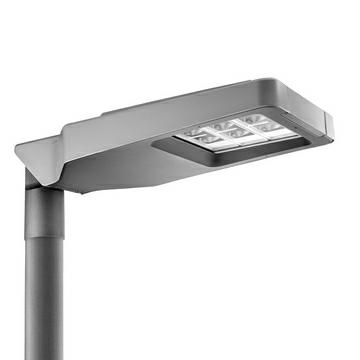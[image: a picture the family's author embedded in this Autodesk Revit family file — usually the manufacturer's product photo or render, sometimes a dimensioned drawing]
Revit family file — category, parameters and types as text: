
# Revit family: Lighting-StreetLighting-GEWISS-ROAD[5]MINI-LED_OPTIC_HUGE_CLII
name_source: partatom
category: Apparecchi per illuminazione
units: mm (PartAtom-declared; Revit-internal decimal feet)

## family parameters
Basato su piano di lavoro = No
Condiviso = No
Punto di calcolo locali = No
Quota connettore circolare = Usa diametro
Sempre verticale = Sì
Sorgente d'illuminazione = No
Taglio con vuoti quando caricato = No
Tipo di parte = Normale

## types (35) — shared parameters
Applicazione = External
Carico apparente = 53 VA
Catalogue = LIGHTING
Catalogue Range = ROAD [5]
Commenti sul wattaggio = 53W
Electrocod = 244C
IDF = 99241b9b-65a6-420a-b558-f156d6702ffc
IDT = 71f3a6385bd246d58e1a34223c0a3191
IP degree = IP66
Immagine tipo = GWR5276M.jpg
Insulation class = II
Lamp- = LED
Lampada = LED
Minimum distance from the illuminated object = 1M
Produttore = GEWISS S.p.A.
SEO = Street lighting
Shock resistance = IK08
Technical sheet = https://www.gewiss.com
Tilt adjustable = -20° ÷ +10° side bracket - -10° ÷ +20° pole head
URL = https://www.gewiss.com
Version file RFA = 20.11
Warranty = 5 years

## per-type parameters (varying)
- GWR5172M30K - ROAD5 MINI HUGE 2M 3000K 0,7A CL2 1-10V: Body=Die-cast aluminium -; Classification:=-; Color Rendering Index=CRI-70; Colore=Graphite grey; Colour :=Powder coating; Colour temperature=3000K; Colour temperature:=3000 K (CRI>80); Context=Street and parking lighting; Control System=Dimmable 1-10 V; DIN 18032-3 certification=-; Descrizione=GWR5172M30K - ROAD5 MINI HUGE 2M 3000K 0,7A CL2 1-10V; Device with reduced surface temperature=-; Driver=Included; Driver Box=Built-in; Efficiency (lm/W)=96; Eletrical and lighting features=-; External screw=Stainless steel; Fixing=Pole Head - Outreach; Gasket=Anti-aging silicone; General information=-; Glow Wire Test :=-; IPEA=ROAD = A ++ // LARGE AREAS = A ++ // CYCLOPEDONALS = A + // GREEN AREAS = A + // HISTORICAL CENTER = A5 +; Installationa and maintenance=-; LED Life Time (L80B05)=77000H; LED Maintenance=Not available; LED current.=0,7A; Lifetime=L90B10 (Tq+25°C) = 100.000 h - L90B10 (Tq+50°C) = 75.000 h; Locking Hook=Integrated front handle; Lumen output (lm)=5200; Luminaire=LED Road Equipment; Materials=-; Maximum surface exposed to the wind=0,149999999999999M2; Maximum surface exposed to the wind :=0.15 m²; Modello=GWR5172M30K; Mouting and installation=Pole Head - Outreach; Nominal flux (lm)=5400; Number of modules=2 (2x3 LED); Operating temperature :=-25 +50 °C; Operating temperature:=-25 +50 °C; Optic=HUGE; Optic :=Metallized polycarbonate reflector; Optic Maintenance=Not available; Optic and illuminating features=-; Overvoltage protection=DM 10KV / CM 10KV; Overvoltage resistance :=Common and dfferential mode: 10KV; Photobiological Risk Class=RG0; Power supply operation=Dimmable; Rated frequency (Hz)=50 / 60; Shield type=4mm thick flat tempered glass; Standard Deviation Colour Matching=SDCM = 5; Standard-=EN 60598-2-3, EN 60598-1 IEC/TR 62778; Standards and approvals=-; Stocking temperature=-; Supply voltage=220 - 240 V; System power=53W; System power :=54 W @ 0.7A; Tilt-=-20° ÷ +10° side bracket - -10° ÷ +20° pole head; Tipo alimentatore=Constant Current Driver Led; Tipologia=Dimmable; Type of light source=LED - Not replaceable; Unified Glare Rating=G*3 - ULOR = 0; Unique digital code (Datamatrix)=Currently not present; Voltage-=220/240 V - 50/60 Hz - Dimmable 1-10 V; Weight (kg):=6,6; Wiring=Isolating switch
- GWR5112 - ROAD 5 2M 4000K 1A OPT.ST1: Colour temperature=4000 K (CRI 70); Colour temperature:=4000 K (CRI 70); Descrizione=ROAD 5 2M 4000K 1A OPT.ST1; EAN code=8011564857711; LED LifeTime (L80B05)=120000H; LED current.=1A; Lumen output (lm)=6730; Maximum surface exposed to the wind=0,15M2; Modello=GWR5112; No. Chorus modules=2 (2x3 LED); Nominal flux (lm)=9540; Number of modules=2 (2x3 LED); Operating temperature:=-25 +40 °C; Optic=H - ULOR: 0%; Overvoltage resistance=12 KV (Common and dfferential mode); Pilot current=1A; System power=76W; Tipo alimentatore=Constant Current Driver Led; Tipologia=Stand alone; Voltage-=220/240 V - 50/60 Hz - Stand alone; Weight (kg)=6,6; Weight (kg):=6,6; Working temperature=-25 +40 °C
- GWR5111B - ROAD 5 BI-POW.1M 4000K 1A OPT.ST1: Colour temperature=4000 K (CRI 70); Colour temperature:=4000 K (CRI 70); Descrizione=ROAD 5 BI-POW.1M 4000K 1A OPT.ST1; EAN code=8011564857735; LED LifeTime (L80B05)=120000H; LED current.=1A; Lumen output (lm)=3370; Maximum surface exposed to the wind=0,15M2; Modello=GWR5111B; No. Chorus modules=1 (1x3 LED); Nominal flux (lm)=4770; Number of modules=1 (1x3 LED); Operating temperature:=-25 +40 °C; Optic=H - ULOR: 0%; Overvoltage resistance=12 KV (Common and dfferential mode); Pilot current=1A; Power supply operation=Bi power; System power=39W; Tipo alimentatore=Constant Current Driver Led; Tipologia=Bi power; Voltage-=220/240 V - 50/60 Hz - Bi-power with self-learning; Weight (kg)=6,4; Weight (kg):=6,4; Working temperature=-25 +40 °C
- GWR5112M30K - ROAD5 MINI HUGE 2M 3000K 1,0A CL2 1-10V: Body=Die-cast aluminium -; Classification:=-; Color Rendering Index=CRI-70; Colore=Graphite grey; Colour :=Powder coating; Colour temperature=3000K; Colour temperature:=3000 K (CRI>80); Context=Street and parking lighting; Control System=Dimmable 1-10 V; DIN 18032-3 certification=-; Descrizione=GWR5112M30K - ROAD5 MINI HUGE 2M 3000K 1,0A CL2 1-10V; Device with reduced surface temperature=-; Driver=Included; Driver Box=Built-in; Efficiency (lm/W)=91; Eletrical and lighting features=-; External screw=Stainless steel; Fixing=Pole Head - Outreach; Gasket=Anti-aging silicone; General information=-; Glow Wire Test :=-; IPEA=ROAD = A + // LARGE AREAS = A + // CYCLOPEDONALS = A // GREEN AREAS = A // HISTORICAL CENTER = A4 +; Installationa and maintenance=-; LED Life Time (L80B05)=120000H; LED Maintenance=Not available; LED current.=1A; Lifetime=L90B10 (Tq+25°C) = 100.000 h - L90B10 (Tq+40°C) = 75.000 h; Locking Hook=Integrated front handle; Lumen output (lm)=7000; Luminaire=LED Road Equipment; Materials=-; Maximum surface exposed to the wind=0,149999999999999M2; Maximum surface exposed to the wind :=0.15 m²; Modello=GWR5112M30K; Mouting and installation=Pole Head - Outreach; Nominal flux (lm)=8280; Number of modules=2 (2x3 LED); Operating temperature :=-25 +40 °C; Operating temperature:=-25 +40 °C; Optic=HUGE; Optic :=Metallized polycarbonate reflector; Optic Maintenance=Not available; Optic and illuminating features=-; Overvoltage protection=DM 10KV / CM 10KV; Overvoltage resistance :=Common and dfferential mode: 10KV; Photobiological Risk Class=RG0; Power supply operation=Dimmable; Rated frequency (Hz)=50 / 60; Shield type=4mm thick flat tempered glass; Standard Deviation Colour Matching=SDCM = 5; Standard-=EN 60598-2-3, EN 60598-1 IEC/TR 62778; Standards and approvals=-; Stocking temperature=-; Supply voltage=220 - 240 V; System power=76W; System power :=77 W @ 1A; Tilt-=-20° ÷ +10° side bracket - -10° ÷ +20° pole head; Tipo alimentatore=Constant Current Driver Led; Tipologia=Dimmable; Type of light source=LED - Not replaceable; Unified Glare Rating=G*3 - ULOR = 0; Unique digital code (Datamatrix)=Currently not present; Voltage-=220/240 V - 50/60 Hz - Dimmable 1-10 V; Weight (kg):=6,6; Wiring=Isolating switch
- GWR5171V - ROAD5 MINI HUGE V 1M 4000K 0,7A CL2: Body=Die-cast aluminium -; Classification:=-; Color Rendering Index=CRI-70; Colore=Graphite grey; Colour :=Powder coating; Colour temperature=4000K; Colour temperature:=4000 K (CRI>70); Context=Street and parking lighting; Control System=DALI - 5 Step; DIN 18032-3 certification=-; Descrizione=GWR5171V - ROAD5 MINI HUGE V 1M 4000K 0,7A CL2; Device with reduced surface temperature=-; Driver=Included; Driver Box=Built-in; Efficiency (lm/W)=107; Eletrical and lighting features=-; External screw=Stainless steel; Fixing=Pole Head - Outreach; Gasket=Anti-aging silicone; General information=-; Glow Wire Test :=-; IPEA=ROAD = A3 + // LARGE AREAS = A4 + // CYCLOPEDONALS = A3 + // GREEN AREAS = A3 + // HISTORICAL CENTER = A6 +; Installationa and maintenance=-; LED Life Time (L80B05)=120000H; LED Maintenance=Not available; LED current.=0,7A; Lifetime=L90B10 (Tq+25°C) = 100.000 h - L90B10 (Tq+50°C) = 75.000 h; Locking Hook=Integrated front handle; Lumen output (lm)=3000; Luminaire=LED Road Equipment; Materials=-; Maximum surface exposed to the wind=0,149999999999999M2; Maximum surface exposed to the wind :=0.15 m²; Modello=GWR5171V; Mouting and installation=Pole Head - Outreach; Nominal flux (lm)=3120; Number of modules=1 (1x3 LED); Operating temperature :=-25 +50 °C; Operating temperature:=-25 +40 °C; Optic=HUGE; Optic :=Metallized polycarbonate reflector; Optic Maintenance=Not available; Optic and illuminating features=-; Overvoltage protection=DM 10KV / CM 10KV; Photobiological Risk Class=RG0; Rated frequency (Hz)=50 / 60; Shield type=4mm thick flat tempered glass; Standard Deviation Colour Matching=SDCM = 5; Standard-=EN 60598-2-3, EN 60598-1 IEC/TR 62778; Standards and approvals=-; Stocking temperature=-; Supply voltage=220 - 240 V; System power=27W; System power :=28 W @ 0.7A; Tilt-=-20° ÷ +10° side bracket - -10° ÷ +20° pole head; Tipologia=Programmable (5 step); Type of light source=LED - Not replaceable; Unified Glare Rating=G*3 - ULOR = 0; Unique digital code (Datamatrix)=Currently not present; Voltage-=220/240 V - 50/60 Hz - Stand alone and/or programmable; Weight (kg):=6,4; Wiring=Isolating switch
- GWR5172B - ROAD5 MINI HUGE 2M 4000K 0,7A CL2 BIREG: Colour temperature=4000 K (CRI 70); Colour temperature:=4000 K (CRI 70); Descrizione=ROAD 5 BI-POW.2M 4000K 700mA OPT.ST1; EAN code=8011564857742; LED LifeTime (L80B05)=77000H; LED current.=0,7A; Lumen output (lm)=4590; Maximum surface exposed to the wind=0,15M2; Modello=GWR5172B; No. Chorus modules=2 (2x3 LED); Nominal flux (lm)=6240; Number of modules=2 (2x3 LED); Operating temperature:=-25 +50 °C; Optic=H - ULOR: 0%; Overvoltage resistance=12 KV (Common and dfferential mode); Pilot current=0,7A; Power supply operation=Bi power; System power=54W; Tipo alimentatore=Constant Current Driver Led; Tipologia=Bi power; Voltage-=220/240 V - 50/60 Hz - Bi-power with self-learning; Weight (kg)=6,6; Weight (kg):=6,6; Working temperature=-25 +50 °C
- GWR511230K - ROAD 5 2M 3000K 1A OTT.ST1: Body=Die-cast aluminium -; Classification:=-; Color Rendering Index=CRI-70; Colore=Graphite grey; Colour :=Powder coating; Colour temperature=3000K; Colour temperature:=3000 K (CRI>80); Context=Street and parking lighting; Control System=Stand alone; DIN 18032-3 certification=-; Descrizione=GWR511230K - ROAD 5 2M 3000K 1A OTT.ST1; Device with reduced surface temperature=-; Driver=Included; Driver Box=Built-in; Efficiency (lm/W)=97; Eletrical and lighting features=-; External screw=Stainless steel; Fixing=Pole Head - Outreach; Gasket=Anti-aging silicone; General information=-; Glow Wire Test :=-; IPEA=ROAD = A + // LARGE AREAS = A ++ // CYCLOPEDONALS = A + // GREEN AREAS = A + // HISTORICAL CENTER = A5 +; Installationa and maintenance=-; LED Life Time (L80B05)=120000H; LED Maintenance=Not available; LED current.=0,9A; Lifetime=L90B10 (Tq+25°C) = 100.000 h - L90B10 (Tq+40°C) = 75.000 h; Locking Hook=Integrated front handle; Lumen output (lm)=6500; Luminaire=LED Road Equipment; Materials=-; Maximum surface exposed to the wind=0,149999999999999M2; Maximum surface exposed to the wind :=0.15 m²; Modello=GWR511230K; Mouting and installation=Pole Head - Outreach; Nominal flux (lm)=8280; Number of modules=2 (2x3 LED); Operating temperature :=-25 +40 °C; Operating temperature:=-25 +40 °C; Optic=HUGE; Optic :=Metallized polycarbonate reflector; Optic Maintenance=Not available; Optic and illuminating features=-; Overvoltage protection=DM 10KV / CM 10KV; Overvoltage resistance :=Common and dfferential mode: 10KV; Photobiological Risk Class=RG0; Rated frequency (Hz)=50 / 60; Shield type=4mm thick flat tempered glass; Standard Deviation Colour Matching=SDCM = 5; Standard-=EN 60598-2-3, EN 60598-1 IEC/TR 62778; Standards and approvals=-; Stocking temperature=-; Supply voltage=220 - 240 V; System power=76W; System power :=67 W @ 0.9A; Tilt-=-20° ÷ +10° side bracket - -10° ÷ +20° pole head; Tipo alimentatore=Constant Current Driver Led; Tipologia=Stand alone; Type of light source=LED - Not replaceable; Unified Glare Rating=G*3 - ULOR = 0; Unique digital code (Datamatrix)=Currently not present; Voltage-=220/240 V - 50/60 Hz - Stand alone; Weight (kg):=6,6; Wiring=Isolating switch
- GWR5131 - ROAD5 MINI HUGE 1M 4000K 0,35A CL2: Colour temperature=4000 K (CRI 70); Colour temperature:=4000 K (CRI 70); Descrizione=ROAD5 MINI HUGE 1M 4000K 0,35A CL2; EAN code=8011564874022; LED LifeTime (L80B05)=77000H; LED current.=0,35A; Lumen output (lm)=1150; Maximum surface exposed to the wind=0,15M2; Modello=GWR5131; No. Chorus modules=1 (1x3 LED); Nominal flux (lm)=1560; Number of modules=1 (1x3 LED); Operating temperature:=-25 +50 °C; Optic=H - ULOR: 0%; Overvoltage resistance=12 KV (Common and dfferential mode); Pilot current=0,35A; System power=14W; Tipo alimentatore=Constant Current Driver Led; Tipologia=Stand alone; Voltage-=220/240 V - 50/60 Hz - Stand alone; Weight (kg)=6,4; Weight (kg):=6,4; Working temperature=-25 +50 °C
- GWR5112B - ROAD 5 BI-POW.2M 4000K 1A OPT.ST1: Colour temperature=4000 K (CRI 70); Colour temperature:=4000 K (CRI 70); Descrizione=ROAD 5 BI-POW.2M 4000K 1A OPT.ST1; EAN code=8011564857759; LED LifeTime (L80B05)=120000H; LED current.=1A; Lumen output (lm)=6730; Maximum surface exposed to the wind=0,15M2; Modello=GWR5112B; No. Chorus modules=2 (2x3 LED); Nominal flux (lm)=9540; Number of modules=2 (2x3 LED); Operating temperature:=-25 +40 °C; Optic=H - ULOR: 0%; Overvoltage resistance=12 KV (Common and dfferential mode); Pilot current=1A; Power supply operation=Bi power; System power=77W; Tipo alimentatore=Constant Current Driver Led; Tipologia=Bi power; Voltage-=220/240 V - 50/60 Hz - Bi-power with self-learning; Weight (kg)=6,6; Weight (kg):=6,6; Working temperature=-25 +40 °C
- GWR5172B30K - ROAD5 MINI HUGE 2M 3000K 0,7A CL2 BIREG: Body=Die-cast aluminium -; Classification:=-; Color Rendering Index=CRI-70; Colore=Graphite grey; Colour :=Powder coating; Colour temperature=3000K; Colour temperature:=3000 K (CRI>80); Context=Street and parking lighting; Control System=Bi-power with self-learning; DIN 18032-3 certification=-; Descrizione=GWR5172B30K - ROAD5 MINI HUGE 2M 3000K 0,7A CL2 BIREG; Device with reduced surface temperature=-; Driver=Included; Driver Box=Built-in; Efficiency (lm/W)=96; Eletrical and lighting features=-; External screw=Stainless steel; Fixing=Pole Head - Outreach; Gasket=Anti-aging silicone; General information=-; Glow Wire Test :=-; IPEA=ROAD = A ++ // LARGE AREAS = A ++ // CYCLOPEDONALS = A + // GREEN AREAS = A + // HISTORICAL CENTER = A5 +; Installationa and maintenance=-; LED Life Time (L80B05)=77000H; LED Maintenance=Not available; LED current.=0,7A; Lifetime=L90B10 (Tq+25°C) = 100.000 h - L90B10 (Tq+50°C) = 75.000 h; Locking Hook=Integrated front handle; Lumen output (lm)=5200; Luminaire=LED Road Equipment; Materials=-; Maximum surface exposed to the wind=0,149999999999999M2; Maximum surface exposed to the wind :=0.15 m²; Modello=GWR5172B30K; Mouting and installation=Pole Head - Outreach; Nominal flux (lm)=5400; Number of modules=2 (2x3 LED); Operating temperature :=-25 +50 °C; Operating temperature:=-25 +50 °C; Optic=HUGE; Optic :=Metallized polycarbonate reflector; Optic Maintenance=Not available; Optic and illuminating features=-; Overvoltage protection=DM 10KV / CM 10KV; Overvoltage resistance :=Common and dfferential mode: 10KV; Photobiological Risk Class=RG0; Power supply operation=Bi power; Rated frequency (Hz)=50 / 60; Shield type=4mm thick flat tempered glass; Standard Deviation Colour Matching=SDCM = 5; Standard-=EN 60598-2-3, EN 60598-1 IEC/TR 62778; Standards and approvals=-; Stocking temperature=-; Supply voltage=220 - 240 V; System power=54W; System power :=54 W @ 0.7A; Tilt-=-20° ÷ +10° side bracket - -10° ÷ +20° pole head; Tipo alimentatore=Constant Current Driver Led; Tipologia=Bi power; Type of light source=LED - Not replaceable; Unified Glare Rating=G*3 - ULOR = 0; Unique digital code (Datamatrix)=Currently not present; Voltage-=220/240 V - 50/60 Hz - Bi-power with self-learning; Weight (kg):=6,6; Wiring=Isolating switch
- GWR517230K - ROAD5 MINI HUGE 2M 3000K 0,7A CL2: Body=Die-cast aluminium -; Classification:=-; Color Rendering Index=CRI-70; Colore=Graphite grey; Colour :=Powder coating; Colour temperature=3000K; Colour temperature:=3000 K (CRI>80); Context=Street and parking lighting; Control System=Stand alone; DIN 18032-3 certification=-; Descrizione=GWR517230K - ROAD5 MINI HUGE 2M 3000K 0,7A CL2; Device with reduced surface temperature=-; Driver=Included; Driver Box=Built-in; Efficiency (lm/W)=98; Eletrical and lighting features=-; External screw=Stainless steel; Fixing=Pole Head - Outreach; Gasket=Anti-aging silicone; General information=-; Glow Wire Test :=-; IPEA=ROAD = A ++ // LARGE AREAS = A3 + // CYCLOPEDONALS = A ++ // GREEN AREAS = A ++ // HISTORICAL CENTER = A5 +; Installationa and maintenance=-; LED Life Time (L80B05)=77000H; LED Maintenance=Not available; LED current.=0,7A; Lifetime=L90B10 (Tq+25°C) = 100.000 h - L90B10 (Tq+50°C) = 75.000 h; Locking Hook=Integrated front handle; Lumen output (lm)=5200; Luminaire=LED Road Equipment; Materials=-; Maximum surface exposed to the wind=0,149999999999999M2; Maximum surface exposed to the wind :=0.15 m²; Modello=GWR517230K; Mouting and installation=Pole Head - Outreach; Nominal flux (lm)=5400; Number of modules=2 (2x3 LED); Operating temperature :=-25 +50 °C; Operating temperature:=-25 +50 °C; Optic=HUGE; Optic :=Metallized polycarbonate reflector; Optic Maintenance=Not available; Optic and illuminating features=-; Overvoltage protection=DM 10KV / CM 10KV; Overvoltage resistance :=Common and dfferential mode: 10KV; Photobiological Risk Class=RG0; Rated frequency (Hz)=50 / 60; Shield type=4mm thick flat tempered glass; Standard Deviation Colour Matching=SDCM = 5; Standard-=EN 60598-2-3, EN 60598-1 IEC/TR 62778; Standards and approvals=-; Stocking temperature=-; Supply voltage=220 - 240 V; System power=53W; System power :=53 W @ 0.7A; Tilt-=-20° ÷ +10° side bracket - -10° ÷ +20° pole head; Tipo alimentatore=Constant Current Driver Led; Tipologia=Stand alone; Type of light source=LED - Not replaceable; Unified Glare Rating=G*3 - ULOR = 0; Unique digital code (Datamatrix)=Currently not present; Voltage-=220/240 V - 50/60 Hz - Stand alone; Weight (kg):=6,6; Wiring=Isolating switch
- GWR5171B - ROAD5 MINI HUGE 1M 4000K 0,7A CL2 BIREG: Colour temperature=4000 K (CRI 70); Colour temperature:=4000 K (CRI 70); Descrizione=ROAD 5 BI-POW.1M 4000K 700mA OPT.ST1; EAN code=8011564857728; LED LifeTime (L80B05)=77000H; LED current.=0,7A; Lumen output (lm)=2300; Maximum surface exposed to the wind=0,15M2; Modello=GWR5171B; No. Chorus modules=1 (1x3 LED); Nominal flux (lm)=3120; Number of modules=1 (1x3 LED); Operating temperature:=-25 +50 °C; Optic=H - ULOR: 0%; Overvoltage resistance=12 KV (Common and dfferential mode); Pilot current=0,7A; Power supply operation=Bi power; System power=28W; Tipo alimentatore=Constant Current Driver Led; Tipologia=Bi power; Voltage-=220/240 V - 50/60 Hz - Bi-power with self-learning; Weight (kg)=6,4; Weight (kg):=6,4; Working temperature=-25 +50 °C
- GWR5111M - ROAD5 MINI HUGE 1M 4000K 1,0A CL2 1-10V: Colour temperature=4000 K (CRI 70); Colour temperature:=4000 K (CRI 70); Descrizione=ROAD 5 DIMM.1M 4000K 1A OPT.ST1; EAN code=8011564857773; LED LifeTime (L80B05)=120000H; LED current.=1A; Lumen output (lm)=3370; Maximum surface exposed to the wind=0,15M2; Modello=GWR5111M; No. Chorus modules=1 (1x3 LED); Nominal flux (lm)=4770; Number of modules=1 (1x3 LED); Operating temperature:=-25 +40 °C; Optic=H - ULOR: 0%; Overvoltage resistance=12 KV (Common and dfferential mode); Pilot current=1A; Power supply operation=Dimmable; System power=38W; Tipo alimentatore=Constant Current Driver Led; Tipologia=Dimmable; Voltage-=220/240 V - 50/60 Hz - Dimmable 1-10 V; Weight (kg)=6,4; Weight (kg):=6,4; Working temperature=-25 +40 °C
- GWR511130K - ROAD 5 1M 3000K 1A OTT.ST1: Body=Die-cast aluminium -; Classification:=-; Color Rendering Index=CRI-70; Colore=Graphite grey; Colour :=Powder coating; Colour temperature=3000K; Colour temperature:=3000 K (CRI>80); Context=Street and parking lighting; Control System=Stand alone; DIN 18032-3 certification=-; Descrizione=GWR511130K - ROAD 5 1M 3000K 1A OTT.ST1; Device with reduced surface temperature=-; Driver=Included; Driver Box=Built-in; Efficiency (lm/W)=92; Eletrical and lighting features=-; External screw=Stainless steel; Fixing=Pole Head - Outreach; Gasket=Anti-aging silicone; General information=-; Glow Wire Test :=-; IPEA=ROAD = A + // LARGE AREAS = A ++ // CYCLOPEDONALS = A + // GREEN AREAS = A + // HISTORICAL CENTER = A4 +; Installationa and maintenance=-; LED Life Time (L80B05)=120000H; LED Maintenance=Not available; LED current.=1A; Lifetime=L90B10 (Tq+25°C) = 100.000 h - L90B10 (Tq+40°C) = 75.000 h; Locking Hook=Integrated front handle; Lumen output (lm)=3500; Luminaire=LED Road Equipment; Materials=-; Maximum surface exposed to the wind=0,149999999999999M2; Maximum surface exposed to the wind :=0.15 m²; Modello=GWR511130K; Mouting and installation=Pole Head - Outreach; Nominal flux (lm)=4140; Number of modules=1 (1x3 LED); Operating temperature :=-25 +40 °C; Operating temperature:=-25 +40 °C; Optic=HUGE; Optic :=Metallized polycarbonate reflector; Optic Maintenance=Not available; Optic and illuminating features=-; Overvoltage protection=DM 10KV / CM 10KV; Overvoltage resistance :=Common and dfferential mode: 10KV; Photobiological Risk Class=RG0; Rated frequency (Hz)=50 / 60; Shield type=4mm thick flat tempered glass; Standard Deviation Colour Matching=SDCM = 5; Standard-=EN 60598-2-3, EN 60598-1 IEC/TR 62778; Standards and approvals=-; Stocking temperature=-; Supply voltage=220 - 240 V; System power=38W; System power :=38 W @ 1A; Tilt-=-20° ÷ +10° side bracket - -10° ÷ +20° pole head; Tipo alimentatore=Constant Current Driver Led; Tipologia=Stand alone; Type of light source=LED - Not replaceable; Unified Glare Rating=G*3 - ULOR = 0; Unique digital code (Datamatrix)=Currently not present; Voltage-=220/240 V - 50/60 Hz - Stand alone; Weight (kg):=6,4; Wiring=Isolating switch
- GWR5171 - ROAD 5 1M 4000K 700mA OPT.ST1: Colour temperature=4000 K (CRI 70); Colour temperature:=4000 K (CRI 70); Descrizione=ROAD 5 1M 4000K 700mA OPT.ST1; EAN code=8011564857377; LED LifeTime (L80B05)=77000H; LED current.=0,7A; Lumen output (lm)=2300; Maximum surface exposed to the wind=0,15M2; Modello=GWR5171; No. Chorus modules=1 (1x3 LED); Nominal flux (lm)=3120; Number of modules=1 (1x3 LED); Operating temperature:=-25 +50 °C; Optic=H - ULOR: 0%; Overvoltage resistance=12 KV (Common and dfferential mode); Pilot current=0,7A; System power=27W; Tipo alimentatore=Constant Current Driver Led; Tipologia=Stand alone; Voltage-=220/240 V - 50/60 Hz - Stand alone; Weight (kg)=6,4; Weight (kg):=6,4; Working temperature=-25 +50 °C
- GWR5171M - ROAD5 MINI HUGE 1M 4000K 0,7A CL2 1-10V: Colour temperature=4000 K (CRI 70); Colour temperature:=4000 K (CRI 70); Descrizione=ROAD 5 DIMM.1M 4000K 700mA OPT.ST1; EAN code=8011564857766; LED LifeTime (L80B05)=77000H; LED current.=0,7A; Lumen output (lm)=2300; Maximum surface exposed to the wind=0,15M2; Modello=GWR5171M; No. Chorus modules=1 (1x3 LED); Nominal flux (lm)=3120; Number of modules=1 (1x3 LED); Operating temperature:=-25 +50 °C; Optic=H - ULOR: 0%; Overvoltage resistance=12 KV (Common and dfferential mode); Pilot current=0,7A; Power supply operation=Dimmable; System power=27W; Tipo alimentatore=Constant Current Driver Led; Tipologia=Dimmable; Voltage-=220/240 V - 50/60 Hz - Dimmable 1-10 V; Weight (kg)=6,4; Weight (kg):=6,4; Working temperature=-25 +50 °C
- GWR5172M - ROAD5 MINI HUGE 2M 4000K 0,7A CL2 1-10V: Colour temperature=4000 K (CRI 70); Colour temperature:=4000 K (CRI 70); Descrizione=ROAD 5 DIMM.2M 4000K 700mA OPT.ST1; EAN code=8011564857780; LED LifeTime (L80B05)=77000H; LED current.=0,7A; Lumen output (lm)=4590; Maximum surface exposed to the wind=0,15M2; Modello=GWR5172M; No. Chorus modules=2 (2x3 LED); Nominal flux (lm)=6240; Number of modules=2 (2x3 LED); Operating temperature:=-25 +50 °C; Optic=H - ULOR: 0%; Overvoltage resistance=12 KV (Common and dfferential mode); Pilot current=0,7A; Power supply operation=Dimmable; System power=53W; Tipo alimentatore=Constant Current Driver Led; Tipologia=Dimmable; Voltage-=220/240 V - 50/60 Hz - Dimmable 1-10 V; Weight (kg)=6,6; Weight (kg):=6,6; Working temperature=-25 +50 °C
- GWR5131V - ROAD5 MINI HUGE V 1M 4000K 0,35A CL2: Body=Die-cast aluminium -; Classification:=-; Color Rendering Index=CRI-70; Colore=Graphite grey; Colour :=Powder coating; Colour temperature=4000K; Colour temperature:=4000 K (CRI>70); Context=Street and parking lighting; Control System=DALI - 5 Step; DIN 18032-3 certification=-; Descrizione=GWR5131V - ROAD5 MINI HUGE V 1M 4000K 0,35A CL2; Device with reduced surface temperature=-; Driver=Included; Driver Box=Built-in; Efficiency (lm/W)=114; Eletrical and lighting features=-; External screw=Stainless steel; Fixing=Pole Head - Outreach; Gasket=Anti-aging silicone; General information=-; Glow Wire Test :=-; IPEA=ROAD = A4 + // LARGE AREAS = A5 + // CYCLOPEDONALS = A4 + // GREEN AREAS = A4 + // HISTORICAL CENTER = A6 +; Installationa and maintenance=-; LED Life Time (L80B05)=120000H; LED Maintenance=Not available; LED current.=0,35A; Lifetime=L90B10 (Tq+25°C) = 100.000 h - L90B10 (Tq+50°C) = 75.000 h; Locking Hook=Integrated front handle; Lumen output (lm)=1600; Luminaire=LED Road Equipment; Materials=-; Maximum surface exposed to the wind=0,149999999999999M2; Maximum surface exposed to the wind :=0.15 m²; Modello=GWR5131V; Mouting and installation=Pole Head - Outreach; Nominal flux (lm)=1560; Number of modules=1 (1x3 LED); Operating temperature :=-25 +50 °C; Operating temperature:=-25 +40 °C; Optic=HUGE; Optic :=Metallized polycarbonate reflector; Optic Maintenance=Not available; Optic and illuminating features=-; Overvoltage protection=DM 10KV / CM 10KV; Photobiological Risk Class=RG0; Rated frequency (Hz)=50 / 60; Shield type=4mm thick flat tempered glass; Standard Deviation Colour Matching=SDCM = 5; Standard-=EN 60598-2-3, EN 60598-1 IEC/TR 62778; Standards and approvals=-; Stocking temperature=-; Supply voltage=220 - 240 V; System power=14W; System power :=14 W @ 0.35A; Tilt-=-20° ÷ +10° side bracket - -10° ÷ +20° pole head; Tipologia=Programmable (5 step); Type of light source=LED - Not replaceable; Unified Glare Rating=G*3 - ULOR = 0; Unique digital code (Datamatrix)=Currently not present; Voltage-=220/240 V - 50/60 Hz - Stand alone and/or programmable; Weight (kg):=6,4; Wiring=Isolating switch
- GWR5111M30K - ROAD5 MINI HUGE 1M 3000K 1,0A CL2 1-10V: Body=Die-cast aluminium -; Classification:=-; Color Rendering Index=CRI-70; Colore=Graphite grey; Colour :=Powder coating; Colour temperature=3000K; Colour temperature:=3000 K (CRI>80); Context=Street and parking lighting; Control System=Dimmable 1-10 V; DIN 18032-3 certification=-; Descrizione=GWR5111M30K - ROAD5 MINI HUGE 1M 3000K 1,0A CL2 1-10V; Device with reduced surface temperature=-; Driver=Included; Driver Box=Built-in; Efficiency (lm/W)=90; Eletrical and lighting features=-; External screw=Stainless steel; Fixing=Pole Head - Outreach; Gasket=Anti-aging silicone; General information=-; Glow Wire Test :=-; IPEA=ROAD = A + // LARGE AREAS = A + // CYCLOPEDONALS = A // GREEN AREAS = A // HISTORICAL CENTER = A3 +; Installationa and maintenance=-; LED Life Time (L80B05)=120000H; LED Maintenance=Not available; LED current.=1A; Lifetime=L90B10 (Tq+25°C) = 100.000 h - L90B10 (Tq+40°C) = 75.000 h; Locking Hook=Integrated front handle; Lumen output (lm)=3500; Luminaire=LED Road Equipment; Materials=-; Maximum surface exposed to the wind=0,149999999999999M2; Maximum surface exposed to the wind :=0.15 m²; Modello=GWR5111M30K; Mouting and installation=Pole Head - Outreach; Nominal flux (lm)=4140; Number of modules=1 (1x3 LED); Operating temperature :=-25 +40 °C; Operating temperature:=-25 +40 °C; Optic=HUGE; Optic :=Metallized polycarbonate reflector; Optic Maintenance=Not available; Optic and illuminating features=-; Overvoltage protection=DM 10KV / CM 10KV; Overvoltage resistance :=Common and dfferential mode: 10KV; Photobiological Risk Class=RG0; Power supply operation=Dimmable; Rated frequency (Hz)=50 / 60; Shield type=4mm thick flat tempered glass; Standard Deviation Colour Matching=SDCM = 5; Standard-=EN 60598-2-3, EN 60598-1 IEC/TR 62778; Standards and approvals=-; Stocking temperature=-; Supply voltage=220 - 240 V; System power=38W; System power :=39 W @ 1A; Tilt-=-20° ÷ +10° side bracket - -10° ÷ +20° pole head; Tipo alimentatore=Constant Current Driver Led; Tipologia=Dimmable; Type of light source=LED - Not replaceable; Unified Glare Rating=G*3 - ULOR = 0; Unique digital code (Datamatrix)=Currently not present; Voltage-=220/240 V - 50/60 Hz - Dimmable 1-10 V; Weight (kg):=6,4; Wiring=Isolating switch
- GWR5172 - ROAD5 MINI HUGE 2M 4000K 0,7A CL2: Colour temperature=4000 K (CRI 70); Colour temperature:=4000 K (CRI 70); Descrizione=ROAD 5 2M 4000K 700mA OPT.ST1; EAN code=8011564857407; LED LifeTime (L80B05)=77000H; LED current.=0,7A; Lumen output (lm)=4590; Maximum surface exposed to the wind=0,15M2; Modello=GWR5172; No. Chorus modules=2 (2x3 LED); Nominal flux (lm)=6240; Number of modules=2 (2x3 LED); Operating temperature:=-25 +50 °C; Optic=H - ULOR: 0%; Overvoltage resistance=12 KV (Common and dfferential mode); Pilot current=0,7A; System power=53W; Tipo alimentatore=Constant Current Driver Led; Tipologia=Stand alone; Voltage-=220/240 V - 50/60 Hz - Stand alone; Weight (kg)=6,6; Weight (kg):=6,6; Working temperature=-25 +50 °C
- GWR5151M - ROAD5 MINI HUGE 1M 4000K 0,5A CL2 1-10V: Body=Die-cast aluminium -; Classification:=-; Color Rendering Index=CRI-70; Colore=Graphite grey; Colour :=Powder coating; Colour temperature=4000K; Colour temperature:=4000 K (CRI>70); Context=Street and parking lighting; Control System=Dimmable 1-10 V; DIN 18032-3 certification=-; Descrizione=GWR5151M - ROAD5 MINI HUGE 1M 4000K 0,5A CL2 1-10V; Device with reduced surface temperature=-; Driver=Included; Driver Box=Built-in; Efficiency (lm/W)=110; Eletrical and lighting features=-; External screw=Stainless steel; Fixing=Pole Head - Outreach; Gasket=Anti-aging silicone; General information=-; Glow Wire Test :=-; IPEA=ROAD = A4 + // LARGE AREAS = A4 + // CYCLOPEDONALS = A3 + // GREEN AREAS = A3 + // HISTORICAL CENTER = A6 +; Installationa and maintenance=-; LED Life Time (L80B05)=120000H; LED Maintenance=Not available; LED current.=0,5A; Lifetime=L90B10 (Tq+25°C) = 100.000 h - L90B10 (Tq+50°C) = 75.000 h; Locking Hook=Integrated front handle; Lumen output (lm)=2200; Luminaire=LED Road Equipment; Materials=-; Maximum surface exposed to the wind=0,149999999999999M2; Maximum surface exposed to the wind :=0.15 m²; Modello=GWR5151M; Mouting and installation=Pole Head - Outreach; Nominal flux (lm)=2400; Number of modules=1 (1x3 LED); Operating temperature :=-25 +50 °C; Operating temperature:=-25 +40 °C; Optic=HUGE; Optic :=Metallized polycarbonate reflector; Optic Maintenance=Not available; Optic and illuminating features=-; Overvoltage protection=DM 10KV / CM 10KV; Photobiological Risk Class=RG0; Rated frequency (Hz)=50 / 60; Shield type=4mm thick flat tempered glass; Standard Deviation Colour Matching=SDCM = 5; Standard-=EN 60598-2-3, EN 60598-1 IEC/TR 62778; Standards and approvals=-; Stocking temperature=-; Supply voltage=220 - 240 V; System power=18W; System power :=20 W @ 0.5A; Tilt-=-20° ÷ +10° side bracket - -10° ÷ +20° pole head; Tipologia=Dimmable; Type of light source=LED - Not replaceable; Unified Glare Rating=G*3 - ULOR = 0; Unique digital code (Datamatrix)=Currently not present; Voltage-=220/240 V - 50/60 Hz - Dimmable 1-10 V; Weight (kg):=6,4; Wiring=Isolating switch
- GWR5152M - ROAD5 MINI HUGE 2M 4000K 0,5A CL2 1-10V: Body=Die-cast aluminium -; Classification:=-; Color Rendering Index=CRI-70; Colore=Graphite grey; Colour :=Powder coating; Colour temperature=4000K; Colour temperature:=4000 K (CRI>70); Context=Street and parking lighting; Control System=Dimmable 1-10 V; DIN 18032-3 certification=-; Descrizione=GWR5152M - ROAD5 MINI HUGE 2M 4000K 0,5A CL2 1-10V; Device with reduced surface temperature=-; Driver=Included; Driver Box=Built-in; Efficiency (lm/W)=116; Eletrical and lighting features=-; External screw=Stainless steel; Fixing=Pole Head - Outreach; Gasket=Anti-aging silicone; General information=-; Glow Wire Test :=-; IPEA=ROAD = A4 + // LARGE AREAS = A5 + // CYCLOPEDONALS = A4 + // GREEN AREAS = A4 + // HISTORICAL CENTER = A6 +; Installationa and maintenance=-; LED Life Time (L80B05)=120000H; LED Maintenance=Not available; LED current.=0,5A; Lifetime=L90B10 (Tq+25°C) = 100.000 h - L90B10 (Tq+50°C) = 75.000 h; Locking Hook=Integrated front handle; Lumen output (lm)=4400; Luminaire=LED Road Equipment; Materials=-; Maximum surface exposed to the wind=0,149999999999999M2; Maximum surface exposed to the wind :=0.15 m²; Modello=GWR5152M; Mouting and installation=Pole Head - Outreach; Nominal flux (lm)=4800; Number of modules=2 (2x3 LED); Operating temperature :=-25 +50 °C; Operating temperature:=-25 +40 °C; Optic=HUGE; Optic :=Metallized polycarbonate reflector; Optic Maintenance=Not available; Optic and illuminating features=-; Overvoltage protection=DM 10KV / CM 10KV; Photobiological Risk Class=RG0; Rated frequency (Hz)=50 / 60; Shield type=4mm thick flat tempered glass; Standard Deviation Colour Matching=SDCM = 5; Standard-=EN 60598-2-3, EN 60598-1 IEC/TR 62778; Standards and approvals=-; Stocking temperature=-; Supply voltage=220 - 240 V; System power=36W; System power :=38 W @ 0.5A; Tilt-=-20° ÷ +10° side bracket - -10° ÷ +20° pole head; Tipologia=Dimmable; Type of light source=LED - Not replaceable; Unified Glare Rating=G*3 - ULOR = 0; Unique digital code (Datamatrix)=Currently not present; Voltage-=220/240 V - 50/60 Hz - Dimmable 1-10 V; Weight (kg):=6,6; Wiring=Isolating switch
- GWR517130K - ROAD5 MINI HUGE 1M 3000K 0,7A CL2: Body=Die-cast aluminium -; Classification:=-; Color Rendering Index=CRI-70; Colore=Graphite grey; Colour :=Powder coating; Colour temperature=3000K; Colour temperature:=3000 K (CRI>80); Context=Street and parking lighting; Control System=Stand alone; DIN 18032-3 certification=-; Descrizione=GWR517130K - ROAD5 MINI HUGE 1M 3000K 0,7A CL2; Device with reduced surface temperature=-; Driver=Included; Driver Box=Built-in; Efficiency (lm/W)=96; Eletrical and lighting features=-; External screw=Stainless steel; Fixing=Pole Head - Outreach; Gasket=Anti-aging silicone; General information=-; Glow Wire Test :=-; IPEA=ROAD = A ++ // LARGE AREAS = A ++ // CYCLOPEDONALS = A + // GREEN AREAS = A + // HISTORICAL CENTER = A5 +; Installationa and maintenance=-; LED Life Time (L80B05)=77000H; LED Maintenance=Not available; LED current.=0,7A; Lifetime=L90B10 (Tq+25°C) = 100.000 h - L90B10 (Tq+50°C) = 75.000 h; Locking Hook=Integrated front handle; Lumen output (lm)=2600; Luminaire=LED Road Equipment; Materials=-; Maximum surface exposed to the wind=0,149999999999999M2; Maximum surface exposed to the wind :=0.15 m²; Modello=GWR517130K; Mouting and installation=Pole Head - Outreach; Nominal flux (lm)=2700; Number of modules=1 (1x3 LED); Operating temperature :=-25 +50 °C; Operating temperature:=-25 +50 °C; Optic=HUGE; Optic :=Metallized polycarbonate reflector; Optic Maintenance=Not available; Optic and illuminating features=-; Overvoltage protection=DM 10KV / CM 10KV; Overvoltage resistance :=Common and dfferential mode: 10KV; Photobiological Risk Class=RG0; Rated frequency (Hz)=50 / 60; Shield type=4mm thick flat tempered glass; Standard Deviation Colour Matching=SDCM = 5; Standard-=EN 60598-2-3, EN 60598-1 IEC/TR 62778; Standards and approvals=-; Stocking temperature=-; Supply voltage=220 - 240 V; System power=27W; System power :=27 W @ 0.7A; Tilt-=-20° ÷ +10° side bracket - -10° ÷ +20° pole head; Tipo alimentatore=Constant Current Driver Led; Tipologia=Stand alone; Type of light source=LED - Not replaceable; Unified Glare Rating=G*3 - ULOR = 0; Unique digital code (Datamatrix)=Currently not present; Voltage-=220/240 V - 50/60 Hz - Stand alone; Weight (kg):=6,4; Wiring=Isolating switch
- GWR5171B30K - ROAD5 MINI HUGE 1M 3000K 0,7A CL2 BIREG: Body=Die-cast aluminium -; Classification:=-; Color Rendering Index=CRI-70; Colore=Graphite grey; Colour :=Powder coating; Colour temperature=3000K; Colour temperature:=3000 K (CRI>80); Context=Street and parking lighting; Control System=Bi-power with self-learning; DIN 18032-3 certification=-; Descrizione=GWR5171B30K - ROAD5 MINI HUGE 1M 3000K 0,7A CL2 BIREG; Device with reduced surface temperature=-; Driver=Included; Driver Box=Built-in; Efficiency (lm/W)=93; Eletrical and lighting features=-; External screw=Stainless steel; Fixing=Pole Head - Outreach; Gasket=Anti-aging silicone; General information=-; Glow Wire Test :=-; IPEA=ROAD = A + // LARGE AREAS = A ++ // CYCLOPEDONALS = A + // GREEN AREAS = A + // HISTORICAL CENTER = A4 +; Installationa and maintenance=-; LED Life Time (L80B05)=77000H; LED Maintenance=Not available; LED current.=0,7A; Lifetime=L90B10 (Tq+25°C) = 100.000 h - L90B10 (Tq+50°C) = 75.000 h; Locking Hook=Integrated front handle; Lumen output (lm)=2600; Luminaire=LED Road Equipment; Materials=-; Maximum surface exposed to the wind=0,149999999999999M2; Maximum surface exposed to the wind :=0.15 m²; Modello=GWR5171B30K; Mouting and installation=Pole Head - Outreach; Nominal flux (lm)=2700; Number of modules=1 (1x3 LED); Operating temperature :=-25 +50 °C; Operating temperature:=-25 +50 °C; Optic=HUGE; Optic :=Metallized polycarbonate reflector; Optic Maintenance=Not available; Optic and illuminating features=-; Overvoltage protection=DM 10KV / CM 10KV; Overvoltage resistance :=Common and dfferential mode: 10KV; Photobiological Risk Class=RG0; Power supply operation=Bi power; Rated frequency (Hz)=50 / 60; Shield type=4mm thick flat tempered glass; Standard Deviation Colour Matching=SDCM = 5; Standard-=EN 60598-2-3, EN 60598-1 IEC/TR 62778; Standards and approvals=-; Stocking temperature=-; Supply voltage=220 - 240 V; System power=28W; System power :=28 W @ 0.7A; Tilt-=-20° ÷ +10° side bracket - -10° ÷ +20° pole head; Tipo alimentatore=Constant Current Driver Led; Tipologia=Bi power; Type of light source=LED - Not replaceable; Unified Glare Rating=G*3 - ULOR = 0; Unique digital code (Datamatrix)=Currently not present; Voltage-=220/240 V - 50/60 Hz - Bi-power with self-learning; Weight (kg):=6,4; Wiring=Isolating switch
- GWR5112M - ROAD5 MINI HUGE 2M 4000K 1,0A CL2 1-10V: Colour temperature=4000 K (CRI 70); Colour temperature:=4000 K (CRI 70); Descrizione=ROAD 5 DIMM.2M 4000K 1A OPT.ST1; EAN code=8011564857797; LED LifeTime (L80B05)=120000H; LED current.=1A; Lumen output (lm)=6730; Maximum surface exposed to the wind=0,15M2; Modello=GWR5112M; No. Chorus modules=2 (2x3 LED); Nominal flux (lm)=9540; Number of modules=2 (2x3 LED); Operating temperature:=-25 +40 °C; Optic=H - ULOR: 0%; Overvoltage resistance=12 KV (Common and dfferential mode); Pilot current=1A; Power supply operation=Dimmable; System power=76W; Tipo alimentatore=Constant Current Driver Led; Tipologia=Dimmable; Voltage-=220/240 V - 50/60 Hz - Dimmable 1-10 V; Weight (kg)=6,6; Weight (kg):=6,6; Working temperature=-25 +40 °C
- GWR513130K - ROAD5 MINI HUGE 1M 3000K 0,35A CL2: Body=Die-cast aluminium -; Classification:=-; Color Rendering Index=CRI-70; Colore=Graphite grey; Colour :=Powder coating; Colour temperature=3000K; Colour temperature:=3000 K (CRI>80); Context=Street and parking lighting; Control System=Stand alone; DIN 18032-3 certification=-; Descrizione=GWR513130K - ROAD5 MINI HUGE 1M 3000K 0,35A CL2; Device with reduced surface temperature=-; Driver=Included; Driver Box=Built-in; Efficiency (lm/W)=108; Eletrical and lighting features=-; External screw=Stainless steel; Fixing=Pole Head - Outreach; Gasket=Anti-aging silicone; General information=-; Glow Wire Test :=-; IPEA=ROAD = A3 + // LARGE AREAS = A4 + // CYCLOPEDONALS = A3 + // GREEN AREAS = A3 + // HISTORICAL CENTER = A6 +; Installationa and maintenance=-; LED Life Time (L80B05)=77000H; LED Maintenance=Not available; LED current.=0,35A; Lifetime=L90B10 (Tq+25°C) = 100.000 h - L90B10 (Tq+50°C) = 75.000 h; Locking Hook=Integrated front handle; Lumen output (lm)=1400; Luminaire=LED Road Equipment; Materials=-; Maximum surface exposed to the wind=0,149999999999999M2; Maximum surface exposed to the wind :=0.15 m²; Modello=GWR513130K; Mouting and installation=Pole Head - Outreach; Nominal flux (lm)=1350; Number of modules=1 (1x3 LED); Operating temperature :=-25 +50 °C; Operating temperature:=-25 +50 °C; Optic=HUGE; Optic :=Metallized polycarbonate reflector; Optic Maintenance=Not available; Optic and illuminating features=-; Overvoltage protection=DM 10KV / CM 10KV; Overvoltage resistance :=Common and dfferential mode: 10KV; Photobiological Risk Class=RG0; Rated frequency (Hz)=50 / 60; Shield type=4mm thick flat tempered glass; Standard Deviation Colour Matching=SDCM = 5; Standard-=EN 60598-2-3, EN 60598-1 IEC/TR 62778; Standards and approvals=-; Stocking temperature=-; Supply voltage=220 - 240 V; System power=14W; System power :=13 W @ 0.35A; Tilt-=-20° ÷ +10° side bracket - -10° ÷ +20° pole head; Tipo alimentatore=Constant Current Driver Led; Tipologia=Stand alone; Type of light source=LED - Not replaceable; Unified Glare Rating=G*3 - ULOR = 0; Unique digital code (Datamatrix)=Currently not present; Voltage-=220/240 V - 50/60 Hz - Stand alone; Weight (kg):=6,4; Wiring=Isolating switch
- GWR5152B - ROAD5 MINI HUGE 2M 4000K 0,5A CL2 BIREG: Body=Die-cast aluminium -; Classification:=-; Color Rendering Index=CRI-70; Colore=Graphite grey; Colour :=Powder coating; Colour temperature=4000K; Colour temperature:=4000 K (CRI>70); Context=Street and parking lighting; Control System=Bi-power with self-learning; DIN 18032-3 certification=-; Descrizione=GWR5152B - ROAD5 MINI HUGE 2M 4000K 0,5A CL2 BIREG; Device with reduced surface temperature=-; Driver=Included; Driver Box=Built-in; Efficiency (lm/W)=116; Eletrical and lighting features=-; External screw=Stainless steel; Fixing=Pole Head - Outreach; Gasket=Anti-aging silicone; General information=-; Glow Wire Test :=-; IPEA=ROAD = A4 + // LARGE AREAS = A5 + // CYCLOPEDONALS = A4 + // GREEN AREAS = A4 + // HISTORICAL CENTER = A6 +; Installationa and maintenance=-; LED Life Time (L80B05)=120000H; LED Maintenance=Not available; LED current.=0,5A; Lifetime=L90B10 (Tq+25°C) = 100.000 h - L90B10 (Tq+50°C) = 75.000 h; Locking Hook=Integrated front handle; Lumen output (lm)=4400; Luminaire=LED Road Equipment; Materials=-; Maximum surface exposed to the wind=0,149999999999999M2; Maximum surface exposed to the wind :=0.15 m²; Modello=GWR5152B; Mouting and installation=Pole Head - Outreach; Nominal flux (lm)=4800; Number of modules=2 (2x3 LED); Operating temperature :=-25 +50 °C; Operating temperature:=-25 +40 °C; Optic=HUGE; Optic :=Metallized polycarbonate reflector; Optic Maintenance=Not available; Optic and illuminating features=-; Overvoltage protection=DM 10KV / CM 10KV; Photobiological Risk Class=RG0; Power supply operation=Bi power; Rated frequency (Hz)=50 / 60; Shield type=4mm thick flat tempered glass; Standard Deviation Colour Matching=SDCM = 5; Standard-=EN 60598-2-3, EN 60598-1 IEC/TR 62778; Standards and approvals=-; Stocking temperature=-; Supply voltage=220 - 240 V; System power=36W; System power :=38 W @ 0.5A; Tilt-=-20° ÷ +10° side bracket - -10° ÷ +20° pole head; Type of light source=LED - Not replaceable; Unified Glare Rating=G*3 - ULOR = 0; Unique digital code (Datamatrix)=Currently not present; Voltage-=220/240 V - 50/60 Hz - Bi-power with self-learning; Weight (kg):=6,6; Wiring=Isolating switch
- GWR5112B30K - ROAD5 MINI HUGE 2M 3000K 1,0A CL2 BIREG: Body=Die-cast aluminium -; Classification:=-; Color Rendering Index=CRI-70; Colore=Graphite grey; Colour :=Powder coating; Colour temperature=3000K; Colour temperature:=3000 K (CRI>80); Context=Street and parking lighting; Control System=Bi-power with self-learning; DIN 18032-3 certification=-; Descrizione=GWR5112B30K - ROAD5 MINI HUGE 2M 3000K 1,0A CL2 BIREG; Device with reduced surface temperature=-; Driver=Included; Driver Box=Built-in; Efficiency (lm/W)=91; Eletrical and lighting features=-; External screw=Stainless steel; Fixing=Pole Head - Outreach; Gasket=Anti-aging silicone; General information=-; Glow Wire Test :=-; IPEA=ROAD = A + // LARGE AREAS = A + // CYCLOPEDONALS = A // GREEN AREAS = A // HISTORICAL CENTER = A4 +; Installationa and maintenance=-; LED Life Time (L80B05)=120000H; LED Maintenance=Not available; LED current.=1A; Lifetime=L90B10 (Tq+25°C) = 100.000 h - L90B10 (Tq+40°C) = 75.000 h; Locking Hook=Integrated front handle; Lumen output (lm)=7000; Luminaire=LED Road Equipment; Materials=-; Maximum surface exposed to the wind=0,149999999999999M2; Maximum surface exposed to the wind :=0.15 m²; Modello=GWR5112B30K; Mouting and installation=Pole Head - Outreach; Nominal flux (lm)=8280; Number of modules=2 (2x3 LED); Operating temperature :=-25 +40 °C; Operating temperature:=-25 +40 °C; Optic=HUGE; Optic :=Metallized polycarbonate reflector; Optic Maintenance=Not available; Optic and illuminating features=-; Overvoltage protection=DM 10KV / CM 10KV; Overvoltage resistance :=Common and dfferential mode: 10KV; Photobiological Risk Class=RG0; Power supply operation=Bi power; Rated frequency (Hz)=50 / 60; Shield type=4mm thick flat tempered glass; Standard Deviation Colour Matching=SDCM = 5; Standard-=EN 60598-2-3, EN 60598-1 IEC/TR 62778; Standards and approvals=-; Stocking temperature=-; Supply voltage=220 - 240 V; System power=77W; System power :=77 W @ 1A; Tilt-=-20° ÷ +10° side bracket - -10° ÷ +20° pole head; Tipo alimentatore=Constant Current Driver Led; Tipologia=Bi power; Type of light source=LED - Not replaceable; Unified Glare Rating=G*3 - ULOR = 0; Unique digital code (Datamatrix)=Currently not present; Voltage-=220/240 V - 50/60 Hz - Bi-power with self-learning; Weight (kg):=6,6; Wiring=Isolating switch
- GWR5111 - ROAD 5 1M 4000K 1A OPT.ST1: Colour temperature=4000 K (CRI 70); Colour temperature:=4000 K (CRI 70); Descrizione=ROAD 5 1M 4000K 1A OPT.ST1; EAN code=8011564857384; LED LifeTime (L80B05)=120000H; LED current.=1A; Lumen output (lm)=3370; Maximum surface exposed to the wind=0,15M2; Modello=GWR5111; No. Chorus modules=1 (1x3 LED); Nominal flux (lm)=4770; Number of modules=1 (1x3 LED); Operating temperature:=-25 +40 °C; Optic=H - ULOR: 0%; Overvoltage resistance=12 KV (Common and dfferential mode); Pilot current=1A; System power=38W; Tipo alimentatore=Constant Current Driver Led; Tipologia=Stand alone; Voltage-=220/240 V - 50/60 Hz - Stand alone; Weight (kg)=6,4; Weight (kg):=6,4; Working temperature=-25 +40 °C
- GWR5172V - ROAD5 MINI HUGE V 2M 4000K 0,7A CL2: Body=Die-cast aluminium -; Classification:=-; Color Rendering Index=CRI-70; Colore=Graphite grey; Colour :=Powder coating; Colour temperature=4000K; Colour temperature:=4000 K (CRI>70); Context=Street and parking lighting; Control System=DALI - 5 Step; DIN 18032-3 certification=-; Descrizione=GWR5172V - ROAD5 MINI HUGE V 2M 4000K 0,7A CL2; Device with reduced surface temperature=-; Driver=Included; Driver Box=Built-in; Efficiency (lm/W)=111; Eletrical and lighting features=-; External screw=Stainless steel; Fixing=Pole Head - Outreach; Gasket=Anti-aging silicone; General information=-; Glow Wire Test :=-; IPEA=ROAD = A4 + // LARGE AREAS = A4 + // CYCLOPEDONALS = A3 + // GREEN AREAS = A3 + // HISTORICAL CENTER = A6 +; Installationa and maintenance=-; LED Life Time (L80B05)=120000H; LED Maintenance=Not available; LED current.=0,7A; Lifetime=L90B10 (Tq+25°C) = 100.000 h - L90B10 (Tq+50°C) = 75.000 h; Locking Hook=Integrated front handle; Lumen output (lm)=6000; Luminaire=LED Road Equipment; Materials=-; Maximum surface exposed to the wind=0,149999999999999M2; Maximum surface exposed to the wind :=0.15 m²; Modello=GWR5172V; Mouting and installation=Pole Head - Outreach; Nominal flux (lm)=6240; Number of modules=2 (2x3 LED); Operating temperature :=-25 +50 °C; Operating temperature:=-25 +40 °C; Optic=HUGE; Optic :=Metallized polycarbonate reflector; Optic Maintenance=Not available; Optic and illuminating features=-; Overvoltage protection=DM 10KV / CM 10KV; Photobiological Risk Class=RG0; Rated frequency (Hz)=50 / 60; Shield type=4mm thick flat tempered glass; Standard Deviation Colour Matching=SDCM = 5; Standard-=EN 60598-2-3, EN 60598-1 IEC/TR 62778; Standards and approvals=-; Stocking temperature=-; Supply voltage=220 - 240 V; System power=53W; System power :=54 W @ 0.7A; Tilt-=-20° ÷ +10° side bracket - -10° ÷ +20° pole head; Tipologia=Programmable (5 step); Type of light source=LED - Not replaceable; Unified Glare Rating=G*3 - ULOR = 0; Unique digital code (Datamatrix)=Currently not present; Voltage-=220/240 V - 50/60 Hz - Stand alone and/or programmable; Weight (kg):=6,6; Wiring=Isolating switch
- GWR5111B30K - ROAD5 MINI HUGE 1M 3000K 1,0A CL2 BIREG: Body=Die-cast aluminium -; Classification:=-; Color Rendering Index=CRI-70; Colore=Graphite grey; Colour :=Powder coating; Colour temperature=3000K; Colour temperature:=3000 K (CRI>80); Context=Street and parking lighting; Control System=Bi-power with self-learning; DIN 18032-3 certification=-; Descrizione=GWR5111B30K - ROAD5 MINI HUGE 1M 3000K 1,0A CL2 BIREG; Device with reduced surface temperature=-; Driver=Included; Driver Box=Built-in; Efficiency (lm/W)=90; Eletrical and lighting features=-; External screw=Stainless steel; Fixing=Pole Head - Outreach; Gasket=Anti-aging silicone; General information=-; Glow Wire Test :=-; IPEA=ROAD = A + // LARGE AREAS = A + // CYCLOPEDONALS = A // GREEN AREAS = A // HISTORICAL CENTER = A3 +; Installationa and maintenance=-; LED Life Time (L80B05)=120000H; LED Maintenance=Not available; LED current.=1A; Lifetime=L90B10 (Tq+25°C) = 100.000 h - L90B10 (Tq+40°C) = 75.000 h; Locking Hook=Integrated front handle; Lumen output (lm)=3500; Luminaire=LED Road Equipment; Materials=-; Maximum surface exposed to the wind=0,149999999999999M2; Maximum surface exposed to the wind :=0.15 m²; Modello=GWR5111B30K; Mouting and installation=Pole Head - Outreach; Nominal flux (lm)=4140; Number of modules=1 (1x3 LED); Operating temperature :=-25 +40 °C; Operating temperature:=-25 +40 °C; Optic=HUGE; Optic :=Metallized polycarbonate reflector; Optic Maintenance=Not available; Optic and illuminating features=-; Overvoltage protection=DM 10KV / CM 10KV; Overvoltage resistance :=Common and dfferential mode: 10KV; Photobiological Risk Class=RG0; Power supply operation=Bi power; Rated frequency (Hz)=50 / 60; Shield type=4mm thick flat tempered glass; Standard Deviation Colour Matching=SDCM = 5; Standard-=EN 60598-2-3, EN 60598-1 IEC/TR 62778; Standards and approvals=-; Stocking temperature=-; Supply voltage=220 - 240 V; System power=39W; System power :=39 W @ 1A; Tilt-=-20° ÷ +10° side bracket - -10° ÷ +20° pole head; Tipo alimentatore=Constant Current Driver Led; Tipologia=Bi power; Type of light source=LED - Not replaceable; Unified Glare Rating=G*3 - ULOR = 0; Unique digital code (Datamatrix)=Currently not present; Voltage-=220/240 V - 50/60 Hz - Bi-power with self-learning; Weight (kg):=6,4; Wiring=Isolating switch
- GWR5151B - ROAD5 MINI HUGE 1M 4000K 0,5A CL2 BIREG: Body=Die-cast aluminium -; Classification:=-; Color Rendering Index=CRI-70; Colore=Graphite grey; Colour :=Powder coating; Colour temperature=4000K; Colour temperature:=4000 K (CRI>70); Context=Street and parking lighting; Control System=Bi-power with self-learning; DIN 18032-3 certification=-; Descrizione=GWR5151B - ROAD5 MINI HUGE 1M 4000K 0,5A CL2 BIREG; Device with reduced surface temperature=-; Driver=Included; Driver Box=Built-in; Efficiency (lm/W)=110; Eletrical and lighting features=-; External screw=Stainless steel; Fixing=Pole Head - Outreach; Gasket=Anti-aging silicone; General information=-; Glow Wire Test :=-; IPEA=ROAD = A4 + // LARGE AREAS = A4 + // CYCLOPEDONALS = A3 + // GREEN AREAS = A3 + // HISTORICAL CENTER = A6 +; Installationa and maintenance=-; LED Life Time (L80B05)=120000H; LED Maintenance=Not available; LED current.=0,5A; Lifetime=L90B10 (Tq+25°C) = 100.000 h - L90B10 (Tq+50°C) = 75.000 h; Locking Hook=Integrated front handle; Lumen output (lm)=2200; Luminaire=LED Road Equipment; Materials=-; Maximum surface exposed to the wind=0,149999999999999M2; Maximum surface exposed to the wind :=0.15 m²; Modello=GWR5151B; Mouting and installation=Pole Head - Outreach; Nominal flux (lm)=2400; Number of modules=1 (1x3 LED); Operating temperature :=-25 +50 °C; Operating temperature:=-25 +40 °C; Optic=HUGE; Optic :=Metallized polycarbonate reflector; Optic Maintenance=Not available; Optic and illuminating features=-; Overvoltage protection=DM 10KV / CM 10KV; Photobiological Risk Class=RG0; Power supply operation=Bi power; Rated frequency (Hz)=50 / 60; Shield type=4mm thick flat tempered glass; Standard Deviation Colour Matching=SDCM = 5; Standard-=EN 60598-2-3, EN 60598-1 IEC/TR 62778; Standards and approvals=-; Stocking temperature=-; Supply voltage=220 - 240 V; System power=18W; System power :=20 W @ 0.5A; Tilt-=-20° ÷ +10° side bracket - -10° ÷ +20° pole head; Type of light source=LED - Not replaceable; Unified Glare Rating=G*3 - ULOR = 0; Unique digital code (Datamatrix)=Currently not present; Voltage-=220/240 V - 50/60 Hz - Bi-power with self-learning; Weight (kg):=6,4; Wiring=Isolating switch
- GWR5112V - ROAD5 MINI HUGE V 2M 4000K 1,0A CL2: Body=Die-cast aluminium -; Classification:=-; Color Rendering Index=CRI-70; Colore=Graphite grey; Colour :=Powder coating; Colour temperature=4000K; Colour temperature:=4000 K (CRI>70); Context=Street and parking lighting; Control System=DALI - 5 Step; DIN 18032-3 certification=-; Descrizione=GWR5112V - ROAD5 MINI HUGE V 2M 4000K 1,0A CL2; Device with reduced surface temperature=-; Driver=Included; Driver Box=Built-in; Efficiency (lm/W)=105; Eletrical and lighting features=-; External screw=Stainless steel; Fixing=Pole Head - Outreach; Gasket=Anti-aging silicone; General information=-; Glow Wire Test :=-; IPEA=ROAD = A3 + // LARGE AREAS = A4 + // CYCLOPEDONALS = A ++ // GREEN AREAS = A ++ // HISTORICAL CENTER = A6 +; Installationa and maintenance=-; LED Life Time (L80B05)=120000H; LED Maintenance=Not available; LED current.=1A; Lifetime=L90B10 (Tq+25°C) = 100.000 h - L90B10 (Tq+40°C) = 75.000 h; Locking Hook=Integrated front handle; Lumen output (lm)=8100; Luminaire=LED Road Equipment; Materials=-; Maximum surface exposed to the wind=0,149999999999999M2; Maximum surface exposed to the wind :=0.15 m²; Modello=GWR5112V; Mouting and installation=Pole Head - Outreach; Nominal flux (lm)=9540; Number of modules=2 (2x3 LED); Operating temperature :=-25 +40 °C; Operating temperature:=-25 +40 °C; Optic=HUGE; Optic :=Metallized polycarbonate reflector; Optic Maintenance=Not available; Optic and illuminating features=-; Overvoltage protection=DM 10KV / CM 10KV; Photobiological Risk Class=RG0; Rated frequency (Hz)=50 / 60; Shield type=4mm thick flat tempered glass; Standard Deviation Colour Matching=SDCM = 5; Standard-=EN 60598-2-3, EN 60598-1 IEC/TR 62778; Standards and approvals=-; Stocking temperature=-; Supply voltage=220 - 240 V; System power=76W; System power :=77 W @ 1A; Tilt-=-20° ÷ +10° side bracket - -10° ÷ +20° pole head; Tipologia=Programmable (5 step); Type of light source=LED - Not replaceable; Unified Glare Rating=G*3 - ULOR = 0; Unique digital code (Datamatrix)=Currently not present; Voltage-=220/240 V - 50/60 Hz - Stand alone and/or programmable; Weight (kg):=6,6; Wiring=Isolating switch
- GWR5171M30K - ROAD5 MINI HUGE 1M 3000K 0,7A CL2 1-10V: Body=Die-cast aluminium -; Classification:=-; Color Rendering Index=CRI-70; Colore=Graphite grey; Colour :=Powder coating; Colour temperature=3000K; Colour temperature:=3000 K (CRI>80); Context=Street and parking lighting; Control System=Dimmable 1-10 V; DIN 18032-3 certification=-; Descrizione=GWR5171M30K - ROAD5 MINI HUGE 1M 3000K 0,7A CL2 1-10V; Device with reduced surface temperature=-; Driver=Included; Driver Box=Built-in; Efficiency (lm/W)=93; Eletrical and lighting features=-; External screw=Stainless steel; Fixing=Pole Head - Outreach; Gasket=Anti-aging silicone; General information=-; Glow Wire Test :=-; IPEA=ROAD = A + // LARGE AREAS = A ++ // CYCLOPEDONALS = A + // GREEN AREAS = A + // HISTORICAL CENTER = A4 +; Installationa and maintenance=-; LED Life Time (L80B05)=77000H; LED Maintenance=Not available; LED current.=0,7A; Lifetime=L90B10 (Tq+25°C) = 100.000 h - L90B10 (Tq+50°C) = 75.000 h; Locking Hook=Integrated front handle; Lumen output (lm)=2600; Luminaire=LED Road Equipment; Materials=-; Maximum surface exposed to the wind=0,149999999999999M2; Maximum surface exposed to the wind :=0.15 m²; Modello=GWR5171M30K; Mouting and installation=Pole Head - Outreach; Nominal flux (lm)=2700; Number of modules=1 (1x3 LED); Operating temperature :=-25 +50 °C; Operating temperature:=-25 +50 °C; Optic=HUGE; Optic :=Metallized polycarbonate reflector; Optic Maintenance=Not available; Optic and illuminating features=-; Overvoltage protection=DM 10KV / CM 10KV; Overvoltage resistance :=Common and dfferential mode: 10KV; Photobiological Risk Class=RG0; Power supply operation=Dimmable; Rated frequency (Hz)=50 / 60; Shield type=4mm thick flat tempered glass; Standard Deviation Colour Matching=SDCM = 5; Standard-=EN 60598-2-3, EN 60598-1 IEC/TR 62778; Standards and approvals=-; Stocking temperature=-; Supply voltage=220 - 240 V; System power=27W; System power :=28 W @ 0.7A; Tilt-=-20° ÷ +10° side bracket - -10° ÷ +20° pole head; Tipo alimentatore=Constant Current Driver Led; Tipologia=Dimmable; Type of light source=LED - Not replaceable; Unified Glare Rating=G*3 - ULOR = 0; Unique digital code (Datamatrix)=Currently not present; Voltage-=220/240 V - 50/60 Hz - Dimmable 1-10 V; Weight (kg):=6,4; Wiring=Isolating switch
- GWR5111V - ROAD5 MINI HUGE V 1M 4000K 1,0A CL2: Body=Die-cast aluminium -; Classification:=-; Color Rendering Index=CRI-70; Colore=Graphite grey; Colour :=Powder coating; Colour temperature=4000K; Colour temperature:=4000 K (CRI>70); Context=Street and parking lighting; Control System=DALI - 5 Step; DIN 18032-3 certification=-; Descrizione=GWR5111V - ROAD5 MINI HUGE V 1M 4000K 1,0A CL2; Device with reduced surface temperature=-; Driver=Included; Driver Box=Built-in; Efficiency (lm/W)=105; Eletrical and lighting features=-; External screw=Stainless steel; Fixing=Pole Head - Outreach; Gasket=Anti-aging silicone; General information=-; Glow Wire Test :=-; IPEA=ROAD = A3 + // LARGE AREAS = A4 + // CYCLOPEDONALS = A3 + // GREEN AREAS = A3 + // HISTORICAL CENTER = A6 +; Installationa and maintenance=-; LED Life Time (L80B05)=120000H; LED Maintenance=Not available; LED current.=1A; Lifetime=L90B10 (Tq+25°C) = 100.000 h - L90B10 (Tq+40°C) = 75.000 h; Locking Hook=Integrated front handle; Lumen output (lm)=4100; Luminaire=LED Road Equipment; Materials=-; Maximum surface exposed to the wind=0,149999999999999M2; Maximum surface exposed to the wind :=0.15 m²; Modello=GWR5111V; Mouting and installation=Pole Head - Outreach; Nominal flux (lm)=4770; Number of modules=1 (1x3 LED); Operating temperature :=-25 +40 °C; Operating temperature:=-25 +40 °C; Optic=HUGE; Optic :=Metallized polycarbonate reflector; Optic Maintenance=Not available; Optic and illuminating features=-; Overvoltage protection=DM 10KV / CM 10KV; Photobiological Risk Class=RG0; Rated frequency (Hz)=50 / 60; Shield type=4mm thick flat tempered glass; Standard Deviation Colour Matching=SDCM = 5; Standard-=EN 60598-2-3, EN 60598-1 IEC/TR 62778; Standards and approvals=-; Stocking temperature=-; Supply voltage=220 - 240 V; System power=38W; System power :=39 W @ 1A; Tilt-=-20° ÷ +10° side bracket - -10° ÷ +20° pole head; Tipologia=Programmable (5 step); Type of light source=LED - Not replaceable; Unified Glare Rating=G*3 - ULOR = 0; Unique digital code (Datamatrix)=Currently not present; Voltage-=220/240 V - 50/60 Hz - Stand alone and/or programmable; Weight (kg):=6,4; Wiring=Isolating switch
